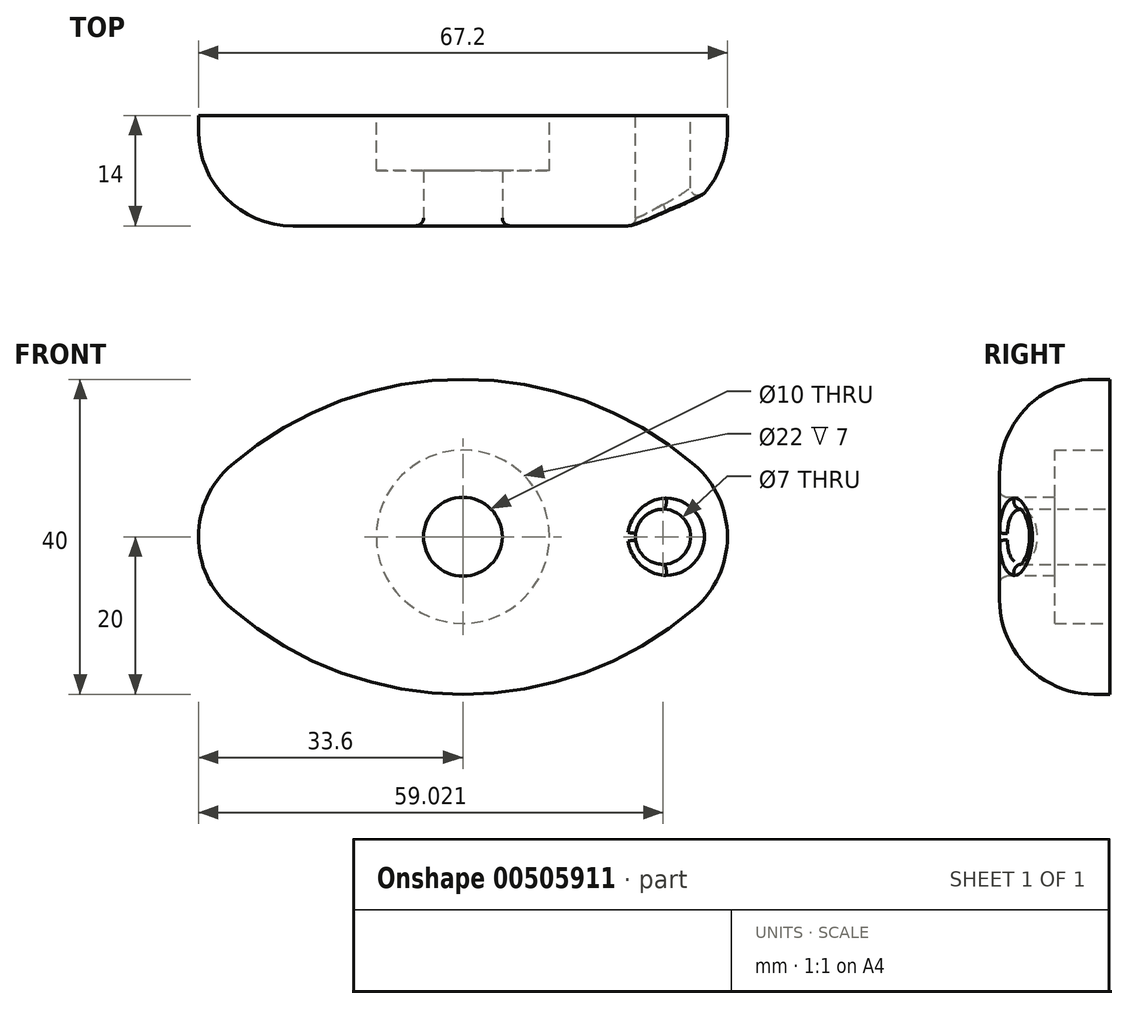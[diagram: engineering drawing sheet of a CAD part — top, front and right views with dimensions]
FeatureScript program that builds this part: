
annotation { "Feature Type Name" : "Feature", "Feature Type Description" : "" }
export const myFeature = defineFeature(function(context is Context, id is Id, definition is map)
    precondition{}
    {
        {
            var Q0;
            Q0=qCreatedBy(makeId("Front.planeOp"),FACE);
            var sketch = newSketch(context, id + "F0", { "sketchPlane" : qUnion([Q0])});
            skCircle(sketch, "E0", {"center": v(0, 0) * mm, "radius": 11 * mm});
            skArc(sketch, "E1", {"start": v(37.5, 0) * mm, "mid": v(0, 20) * mm, "end": v(-37.5, 0) * mm});
            skLineSegment(sketch, "E2", {"start": v(-37.5, 0) * mm, "end": v(37.5, 0) * mm, "construction": true});
            skArc(sketch, "E3.MirrorCS", {"start": v(37.5, 0) * mm, "mid": v(0, -20) * mm, "end": v(-37.5, 0) * mm});
            skLineSegment(sketch, "E4", {"start": v(0, 0) * mm, "end": v(0, -25.16) * mm, "construction": true});
            skSolve(sketch);
        }
        {
            var Q0;
            Q0 = qSketchRegion(id + "F0", true);
            extrude(context, id + "F1", {"entities" : qUnion([Q0]), "depth" : 14 * mm});
        }
        {
            var Q0;
            Q0=makeQuery(id+"F1.opExtrude","CAP_FACE",FACE,{"disambiguationData":[OSD([sQuery(id+"F0.wireOp",EDGE,"E0"),sQuery(id+"F0.wireOp",EDGE,"E1"),sQuery(id+"F0.wireOp",EDGE,"E3.MirrorCS")])],"isStart":false});
            var sketch = newSketch(context, id + "F2", { "sketchPlane" : qUnion([Q0])});
            skCircle(sketch, "E5.0", {"center": v(0, 0) * mm, "radius": 11 * mm});
            skCircle(sketch, "E6", {"center": v(0, 0) * mm, "radius": 5 * mm});
            skSolve(sketch);
        }
        {
            var Q0;
            Q0 = qSketchRegion(id + "F2", true);
            extrude(context, id + "F3", {"entities" : qUnion([Q0]), "operationType" : NewBodyOperationType.ADD, "oppositeDirection" : true, "depth" : 7 * mm});
        }
        {
            var Q0;
            {var subQ0=sQuery(id+"F0.wireOp",EDGE,"E3.MirrorCS");var subQ1=sQuery(id+"F0.wireOp",EDGE,"E1");Q0=makeQuery(id+"F1.opExtrude","SWEPT_EDGE",EDGE,{"disambiguationData":[OSD([subQ1,subQ0]),TDD([makeQuery(id+"F0.imprint","INTERSECT",VERTEX,{"disambiguationData":[OD(1.0)],"derivedFrom":[subQ1,subQ0]})])]});}
            var Q1;
            {var subQ0=sQuery(id+"F0.wireOp",EDGE,"E3.MirrorCS");var subQ1=sQuery(id+"F0.wireOp",EDGE,"E1");Q1=makeQuery(id+"F1.opExtrude","SWEPT_EDGE",EDGE,{"disambiguationData":[OSD([subQ1,subQ0]),TDD([makeQuery(id+"F0.imprint","INTERSECT",VERTEX,{"disambiguationData":[OD(0.0)],"derivedFrom":[subQ1,subQ0]})])]});}
            var Q2;
            Q2=makeQuery(id+"F1.opExtrude","CAP_EDGE",EDGE,{"disambiguationData":[OSD([sQuery(id+"F0.wireOp",EDGE,"E3.MirrorCS")])],"isStart":false});
            var Q3;
            Q3=makeQuery(id+"F1.opExtrude","CAP_EDGE",EDGE,{"disambiguationData":[OSD([sQuery(id+"F0.wireOp",EDGE,"E1")])],"isStart":false});
            fillet(context, id + "F4", {"entities" : qUnion([Q0, Q1, Q2, Q3]), "radius" : 12 * mm, "tangentPropagation" : true, "allowEdgeOverflow" : false});
        }
        {
            var Q0;
            Q0=makeQuery(id+"F1.opExtrude","CAP_FACE",FACE,{"disambiguationData":[OSD([sQuery(id+"F0.wireOp",EDGE,"E0"),sQuery(id+"F0.wireOp",EDGE,"E1"),sQuery(id+"F0.wireOp",EDGE,"E3.MirrorCS")])],"isStart":true});
            var sketch = newSketch(context, id + "F5", { "sketchPlane" : qUnion([Q0])});
            skCircle(sketch, "E7", {"center": v(-25.42, 0) * mm, "radius": 3.5 * mm});
            skSolve(sketch);
        }
        {
            var Q0;
            Q0=makeQuery(id+"F5.imprint","IMPRINT",FACE,{"disambiguationData":[TD([[makeQuery(id+"F5.imprint","IMPRINT",EDGE,{"derivedFrom":sQuery(id+"F5.wireOp",EDGE,"E7")}),1.0]])]});
            extrude(context, id + "F6", {"entities" : qUnion([Q0]), "operationType" : NewBodyOperationType.REMOVE, "endBound" : BoundingType.THROUGH_ALL, "oppositeDirection" : true, "depth" : 25 * mm, "offsetDistance" : 25 * mm});
        }
        {
            var Q0;
            Q0=makeQuery(id+"F6.boolean.opBoolean","INTERSECT",EDGE,{"derivedFrom":[makeQuery(id+"F4.opFillet","BLEND_FACE",FACE,{"disambiguationData":[OSD([sQuery(id+"F0.wireOp",EDGE,"E3.MirrorCS")])]}),makeQuery(id+"F6.opExtrude","SWEPT_FACE",FACE,{"disambiguationData":[OSD([sQuery(id+"F5.wireOp",EDGE,"E7")])]})]});
            var Q1;
            Q1=makeQuery(id+"F6.boolean.opBoolean","INTERSECT",EDGE,{"derivedFrom":[makeQuery(id+"F4.opFillet","BLEND_FACE",FACE,{"disambiguationData":[OSD([sQuery(id+"F0.wireOp",EDGE,"E1")])]}),makeQuery(id+"F6.opExtrude","SWEPT_FACE",FACE,{"disambiguationData":[OSD([sQuery(id+"F5.wireOp",EDGE,"E7")])]})]});
            var Q2;
            {var subQ0=sQuery(id+"F0.wireOp",EDGE,"E3.MirrorCS");var subQ1=sQuery(id+"F0.wireOp",EDGE,"E1");Q2=makeQuery(id+"F6.boolean.opBoolean","INTERSECT",EDGE,{"disambiguationData":[OD(1.0)],"derivedFrom":[makeQuery(id+"F4.opFillet","BLEND_FACE",FACE,{"disambiguationData":[OSD([subQ1,subQ0]),TDD([makeQuery(id+"F1.opExtrude","CAP_VERTEX",VERTEX,{"disambiguationData":[OSD([subQ1,subQ0]),TDD([makeQuery(id+"F0.imprint","INTERSECT",VERTEX,{"disambiguationData":[OD(0.0)],"derivedFrom":[subQ1,subQ0]})])],"isStart":false})])]}),makeQuery(id+"F6.opExtrude","SWEPT_FACE",FACE,{"disambiguationData":[OSD([sQuery(id+"F5.wireOp",EDGE,"E7")])]})]});}
            var Q3;
            Q3=makeQuery(id+"F3.opExtrude","CAP_EDGE",EDGE,{"disambiguationData":[OSD([sQuery(id+"F2.wireOp",EDGE,"E6")])],"isStart":true});
            fillet(context, id + "F7", {"entities" : qUnion([Q0, Q1, Q2, Q3]), "radius" : 1 * mm, "tangentPropagation" : true, "allowEdgeOverflow" : false});
        }
    });
